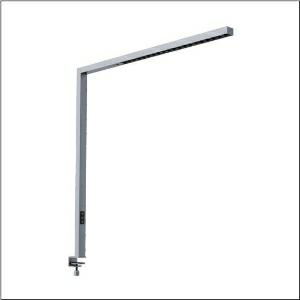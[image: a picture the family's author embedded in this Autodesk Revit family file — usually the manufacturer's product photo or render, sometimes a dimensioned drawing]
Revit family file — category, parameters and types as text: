
# Revit family: silica_31_desk_51my52gatcs
name_source: partatom
category: Lighting Fixtures
units: mm (PartAtom-declared; Revit-internal decimal feet)

## family parameters
Cut with Voids When Loaded = No
Host = Face
Light Source = No
Part Type = Normal
Room Calculation Point = No
Round Connector Dimension = Use Diameter
Shared = No

## types (1)
- --- (1 x LED, 8520 lm, 71 W, 4000K)
    Apparent Load = 71 VA
    CIE Flux Codes = 86 100 100 24 100
    Color Rendering = 80
    Color Temperature = 4000K
    Default Elevation = 1800 mm
    Description = Silica® 31 Desk, desktop luminaire, secondary optical cover: cover panel, of PMMA, light emission: direct/indirect distribution, primary light characteristic: symmetric, installation type: as desk luminaire, LED, rated luminous flux: 8.520lm, luminous efficacy: 120lm/W, light colour: 8tw, colour temperature: 2700..6500K, control gear: Touchdim, daylight-dependent control, with cable with plug, mains connection: 230V, AC, 50Hz, connection cable included, cable length: 2,5m, rated input power: 71W, luminaire head, of aluminium, metallic grey (RAL 9006), length: 1.203mm, width: 52mm, supporting column, angular, of aluminium, metallic grey (RAL 9006), baseplate, of steel, metallic grey (RAL 9006), local control - self-sufficient standalone sensors, direct and indirect component separately switchable, protection rating (complete): IP20, insulation class (complete): insulation class I (protective earthing), certification: CE, ENEC, permissible operating ambient temperature: -20..+40°C, standard: EN 50419, packaging unit: 1 piece
    Height = 36 mm
    Lamp = 1 x LED
    Lamp Light Flux = 8520 lm
    Lamp Power = 71 W
    Lamp count = 1
    Length = 1203 mm
    Luminous efficacy = 120 lm/W
    Manufacturer = Siteco
    ModVariant = No
    Model = 51MY52GATCS
    Mounting Place = Floor
    Mounting Type = Freestanding
    Number of Poles = 1
    OnlyDefault = Yes
    Power Factor = 1
    Product Name = Silica 31 Desk
    Product group = desktop luminaire
    ProductGroupID = 1303
    Protection Class = Protection class I
    Protection Degree = IP 20
    RLX_Detail_Level = 1
    RLX_Emergency_Light_Flux = 0 lm
    RLX_Emergency_Type = 0
    RLX_Emergency_Type_DB = No
    RlxData = <blob elided: 19777 chars, md5=2ca79197>
    Socket = socket
    Standby Power = 0 W
    System Light Flux = 8520 lm
    System Power = 71 W
    Type Comments = factory setting
    Type Image = l_1275333.jpg
    URL = http://relux.com
    VarID = @adj_087099
    Voltage = 0 V
    Weight = 0.00 kg
    Width = 52 mm

## geometry (parser evidence)
native form markers: Blend x4, Sweep x14
no freeform markers — native parametric forms only
